# Revit family: teatime
name_source: partatom
category: Furniture
revit_build: Autodesk Revit 2015 (Build: 20140903_1530(x64)
units: mm (PartAtom-declared; Revit-internal decimal feet)

## types (3) — shared parameters
BIMobject category = Furniture
Date of publishing = 2016-03-22
Design country = Sweden
Edition number = 1
IFC Classification = Furnishing Element
Manufacturer country = Sweden
Manufacturer name = Swedese
Material main = Wood
Nominal height = 760
Nominal width = 750
OmniClass Code = 23-21 11 00
OmniClass Description = Commercial Furniture
Product Guid = 978fc7f5-effb-4763-8c77-bc7339ea9eb6
Product SKU = 27650
Product data url = https://bimobject.com
Product family = Accessories
Product group = Teatime
Product name = Teatime
QR code = http://bimobject.com
Technical description = https://static-swedese.s3.amazonaws.com
UNSPSC Code = 56
Uniclass 1.4 Code = L8211
Uniclass 1.4 Description = Furniture
Weight Net (Kg) = 9
zero-valued in all types: BOSUseNativeGeometries

## type names (no varying parameters)
- COLOUR - (White Wood)
- COLOUR - (Black Wood)
- COLOUR - (Ash Wood)

## geometry (parser evidence)
native form markers: Sweep x2
no freeform markers — native parametric forms only
